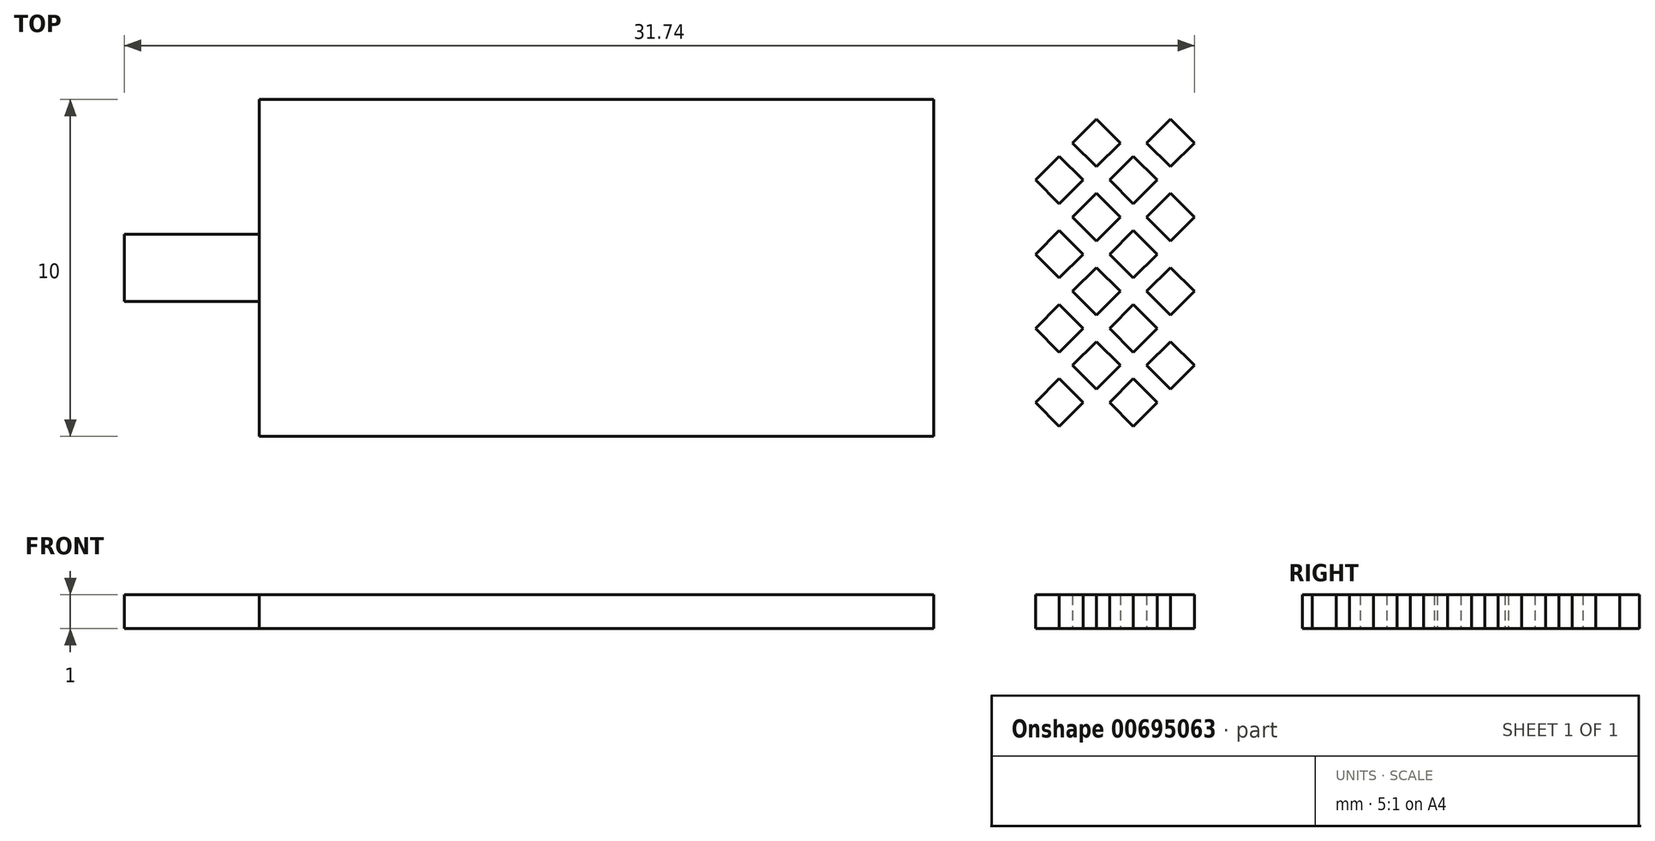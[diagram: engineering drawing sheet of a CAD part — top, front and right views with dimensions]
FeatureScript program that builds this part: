
annotation { "Feature Type Name" : "Feature", "Feature Type Description" : "" }
export const myFeature = defineFeature(function(context is Context, id is Id, definition is map)
    precondition{}
    {
        {
            var Q0;
            Q0=qCreatedBy(makeId("Top.planeOp"),FACE);
            var sketch = newSketch(context, id + "F0", { "sketchPlane" : qUnion([Q0])});
            skLineSegment(sketch, "E0.bottom", {"start": v(0, 0) * mm, "end": v(-20, 0) * mm});
            skLineSegment(sketch, "E0.top", {"start": v(0, 10) * mm, "end": v(-20, 10) * mm});
            skLineSegment(sketch, "E0.left", {"start": v(0, 0) * mm, "end": v(0, 10) * mm});
            skLineSegment(sketch, "E0.right", {"start": v(-20, 0) * mm, "end": v(-20, 10) * mm});
            skSolve(sketch);
        }
        {
            var Q0;
            Q0=qCreatedBy(makeId("Top.planeOp"),FACE);
            var sketch = newSketch(context, id + "F1", { "sketchPlane" : qUnion([Q0])});
            skLineSegment(sketch, "E1.bottom", {"start": v(0, 0) * mm, "end": v(4, 0) * mm});
            skLineSegment(sketch, "E1.top", {"start": v(0, -2) * mm, "end": v(4, -2) * mm});
            skLineSegment(sketch, "E1.left", {"start": v(0, 0) * mm, "end": v(0, -2) * mm});
            skLineSegment(sketch, "E1.right", {"start": v(4, 0) * mm, "end": v(4, -2) * mm});
            skSolve(sketch);
        }
        {
            var Q0;
            Q0=makeQuery(id+"F0.imprint","IMPRINT",FACE,{"disambiguationData":[TD([[makeQuery(id+"F0.imprint","IMPRINT",EDGE,{"derivedFrom":sQuery(id+"F0.wireOp",EDGE,"E0.bottom")}),-1.0]])]});
            extrude(context, id + "F2", {"entities" : qUnion([Q0]), "depth" : 1 * mm, "offsetDistance" : 25 * mm});
        }
        {
            var Q0;
            Q0=makeQuery(id+"F1.imprint","IMPRINT",FACE,{"disambiguationData":[TD([[makeQuery(id+"F1.imprint","IMPRINT",EDGE,{"derivedFrom":sQuery(id+"F1.wireOp",EDGE,"E1.bottom")}),-1.0]])]});
            extrude(context, id + "F3", {"entities" : qUnion([Q0]), "depth" : 1 * mm, "offsetDistance" : 25 * mm});
        }
        {
            var Q0;
            Q0=makeQuery(id+"F3.opExtrude","SWEPT_BODY",BODY,{"disambiguationData":[OSD([sQuery(id+"F1.wireOp",EDGE,"E1.bottom"),sQuery(id+"F1.wireOp",EDGE,"E1.top"),sQuery(id+"F1.wireOp",EDGE,"E1.left"),sQuery(id+"F1.wireOp",EDGE,"E1.right")])]});
            transform(context, id + "F4", {"entities" : qUnion([Q0]), "transformType" : TransformType.TRANSLATION_3D, "dx" : -24 * mm, "dy" : 6 * mm, "dz" : 0 * mm, "makeCopy" : false});
        }
        {
            var Q0;
            Q0=qCreatedBy(makeId("Top.planeOp"),FACE);
            var sketch = newSketch(context, id + "F5", { "sketchPlane" : qUnion([Q0])});
            skLineSegment(sketch, "E2.bottom", {"start": v(3.02, 2) * mm, "end": v(4.02, 2) * mm});
            skLineSegment(sketch, "E2.top", {"start": v(3.02, 1) * mm, "end": v(4.02, 1) * mm});
            skLineSegment(sketch, "E2.left", {"start": v(3.02, 2) * mm, "end": v(3.02, 1) * mm});
            skLineSegment(sketch, "E2.right", {"start": v(4.02, 2) * mm, "end": v(4.02, 1) * mm});
            skSolve(sketch);
        }
        {
            var Q0;
            Q0=makeQuery(id+"F5.imprint","IMPRINT",FACE,{"disambiguationData":[TD([[makeQuery(id+"F5.imprint","IMPRINT",EDGE,{"derivedFrom":sQuery(id+"F5.wireOp",EDGE,"E2.bottom")}),-1.0]])]});
            extrude(context, id + "F6", {"entities" : qUnion([Q0]), "depth" : 1 * mm, "offsetDistance" : 25 * mm});
        }
        {
            var Q0;
            Q0=makeQuery(id+"F6.opExtrude","SWEPT_BODY",BODY,{"disambiguationData":[OSD([sQuery(id+"F5.wireOp",EDGE,"E2.bottom"),sQuery(id+"F5.wireOp",EDGE,"E2.top"),sQuery(id+"F5.wireOp",EDGE,"E2.left"),sQuery(id+"F5.wireOp",EDGE,"E2.right")])]});
            var Q1;
            Q1=makeQuery(id+"F6.opExtrude","SWEPT_EDGE",EDGE,{"disambiguationData":[OSD([sQuery(id+"F5.wireOp",EDGE,"E2.top"),sQuery(id+"F5.wireOp",EDGE,"E2.left")])]});
            transform(context, id + "F7", {"entities" : qUnion([Q0]), "transformType" : TransformType.ROTATION, "transformAxis" : qUnion([Q1]), "angle" : 45 * degree, "makeCopy" : false});
        }
        {
            var Q0;
            Q0=makeQuery(id+"F6.opExtrude","SWEPT_BODY",BODY,{"disambiguationData":[OSD([sQuery(id+"F5.wireOp",EDGE,"E2.bottom"),sQuery(id+"F5.wireOp",EDGE,"E2.top"),sQuery(id+"F5.wireOp",EDGE,"E2.left"),sQuery(id+"F5.wireOp",EDGE,"E2.right")])]});
            transform(context, id + "F8", {"entities" : qUnion([Q0]), "transformType" : TransformType.TRANSLATION_3D, "dx" : 1.1 * mm, "dy" : 1.1 * mm, "dz" : 0 * mm, "makeCopy" : true});
        }
        {
            var Q0;
            Q0=makeQuery(id+"F8.opPattern","COPY",BODY,{"derivedFrom":makeQuery(id+"F6.opExtrude","SWEPT_BODY",BODY,{"disambiguationData":[OSD([sQuery(id+"F5.wireOp",EDGE,"E2.bottom"),sQuery(id+"F5.wireOp",EDGE,"E2.top"),sQuery(id+"F5.wireOp",EDGE,"E2.left"),sQuery(id+"F5.wireOp",EDGE,"E2.right")])]}),"instanceName":"1"});
            transform(context, id + "F9", {"entities" : qUnion([Q0]), "transformType" : TransformType.TRANSLATION_3D, "dx" : -1.1 * mm, "dy" : 1.1 * mm, "dz" : 0 * mm, "makeCopy" : true});
        }
        {
            var Q0;
            Q0=makeQuery(id+"F9.opPattern","COPY",BODY,{"derivedFrom":makeQuery(id+"F8.opPattern","COPY",BODY,{"derivedFrom":makeQuery(id+"F6.opExtrude","SWEPT_BODY",BODY,{"disambiguationData":[OSD([sQuery(id+"F5.wireOp",EDGE,"E2.bottom"),sQuery(id+"F5.wireOp",EDGE,"E2.top"),sQuery(id+"F5.wireOp",EDGE,"E2.left"),sQuery(id+"F5.wireOp",EDGE,"E2.right")])]}),"instanceName":"1"}),"instanceName":"1"});
            var Q1;
            Q1=makeQuery(id+"F8.opPattern","COPY",BODY,{"derivedFrom":makeQuery(id+"F6.opExtrude","SWEPT_BODY",BODY,{"disambiguationData":[OSD([sQuery(id+"F5.wireOp",EDGE,"E2.bottom"),sQuery(id+"F5.wireOp",EDGE,"E2.top"),sQuery(id+"F5.wireOp",EDGE,"E2.left"),sQuery(id+"F5.wireOp",EDGE,"E2.right")])]}),"instanceName":"1"});
            transform(context, id + "F10", {"entities" : qUnion([Q0, Q1]), "transformType" : TransformType.TRANSLATION_3D, "dx" : 0 * mm, "dy" : 2.2 * mm, "dz" : 0 * mm, "makeCopy" : true});
        }
        {
            var Q0;
            Q0=makeQuery(id+"F10.opPattern","COPY",BODY,{"derivedFrom":makeQuery(id+"F9.opPattern","COPY",BODY,{"derivedFrom":makeQuery(id+"F8.opPattern","COPY",BODY,{"derivedFrom":makeQuery(id+"F6.opExtrude","SWEPT_BODY",BODY,{"disambiguationData":[OSD([sQuery(id+"F5.wireOp",EDGE,"E2.bottom"),sQuery(id+"F5.wireOp",EDGE,"E2.top"),sQuery(id+"F5.wireOp",EDGE,"E2.left"),sQuery(id+"F5.wireOp",EDGE,"E2.right")])]}),"instanceName":"1"}),"instanceName":"1"}),"instanceName":"1"});
            var Q1;
            Q1=makeQuery(id+"F10.opPattern","COPY",BODY,{"derivedFrom":makeQuery(id+"F8.opPattern","COPY",BODY,{"derivedFrom":makeQuery(id+"F6.opExtrude","SWEPT_BODY",BODY,{"disambiguationData":[OSD([sQuery(id+"F5.wireOp",EDGE,"E2.bottom"),sQuery(id+"F5.wireOp",EDGE,"E2.top"),sQuery(id+"F5.wireOp",EDGE,"E2.left"),sQuery(id+"F5.wireOp",EDGE,"E2.right")])]}),"instanceName":"1"}),"instanceName":"1"});
            transform(context, id + "F11", {"entities" : qUnion([Q0, Q1]), "transformType" : TransformType.TRANSLATION_3D, "dx" : 0 * mm, "dy" : 2.2 * mm, "dz" : 0 * mm, "makeCopy" : true});
        }
        {
            var Q0;
            Q0=makeQuery(id+"F6.opExtrude","SWEPT_BODY",BODY,{"disambiguationData":[OSD([sQuery(id+"F5.wireOp",EDGE,"E2.bottom"),sQuery(id+"F5.wireOp",EDGE,"E2.top"),sQuery(id+"F5.wireOp",EDGE,"E2.left"),sQuery(id+"F5.wireOp",EDGE,"E2.right")])]});
            transform(context, id + "F12", {"entities" : qUnion([Q0]), "transformType" : TransformType.TRANSLATION_3D, "dx" : 1.1 * mm, "dy" : 7.7 * mm, "dz" : 0 * mm, "makeCopy" : true});
        }
        {
            var Q0;
            Q0=makeQuery(id+"F12.opPattern","COPY",BODY,{"derivedFrom":makeQuery(id+"F6.opExtrude","SWEPT_BODY",BODY,{"disambiguationData":[OSD([sQuery(id+"F5.wireOp",EDGE,"E2.bottom"),sQuery(id+"F5.wireOp",EDGE,"E2.top"),sQuery(id+"F5.wireOp",EDGE,"E2.left"),sQuery(id+"F5.wireOp",EDGE,"E2.right")])]}),"instanceName":"1"});
            var Q1;
            Q1=makeQuery(id+"F11.opPattern","COPY",BODY,{"derivedFrom":makeQuery(id+"F10.opPattern","COPY",BODY,{"derivedFrom":makeQuery(id+"F9.opPattern","COPY",BODY,{"derivedFrom":makeQuery(id+"F8.opPattern","COPY",BODY,{"derivedFrom":makeQuery(id+"F6.opExtrude","SWEPT_BODY",BODY,{"disambiguationData":[OSD([sQuery(id+"F5.wireOp",EDGE,"E2.bottom"),sQuery(id+"F5.wireOp",EDGE,"E2.top"),sQuery(id+"F5.wireOp",EDGE,"E2.left"),sQuery(id+"F5.wireOp",EDGE,"E2.right")])]}),"instanceName":"1"}),"instanceName":"1"}),"instanceName":"1"}),"instanceName":"1"});
            var Q2;
            Q2=makeQuery(id+"F11.opPattern","COPY",BODY,{"derivedFrom":makeQuery(id+"F10.opPattern","COPY",BODY,{"derivedFrom":makeQuery(id+"F8.opPattern","COPY",BODY,{"derivedFrom":makeQuery(id+"F6.opExtrude","SWEPT_BODY",BODY,{"disambiguationData":[OSD([sQuery(id+"F5.wireOp",EDGE,"E2.bottom"),sQuery(id+"F5.wireOp",EDGE,"E2.top"),sQuery(id+"F5.wireOp",EDGE,"E2.left"),sQuery(id+"F5.wireOp",EDGE,"E2.right")])]}),"instanceName":"1"}),"instanceName":"1"}),"instanceName":"1"});
            var Q3;
            Q3=makeQuery(id+"F10.opPattern","COPY",BODY,{"derivedFrom":makeQuery(id+"F9.opPattern","COPY",BODY,{"derivedFrom":makeQuery(id+"F8.opPattern","COPY",BODY,{"derivedFrom":makeQuery(id+"F6.opExtrude","SWEPT_BODY",BODY,{"disambiguationData":[OSD([sQuery(id+"F5.wireOp",EDGE,"E2.bottom"),sQuery(id+"F5.wireOp",EDGE,"E2.top"),sQuery(id+"F5.wireOp",EDGE,"E2.left"),sQuery(id+"F5.wireOp",EDGE,"E2.right")])]}),"instanceName":"1"}),"instanceName":"1"}),"instanceName":"1"});
            var Q4;
            Q4=makeQuery(id+"F10.opPattern","COPY",BODY,{"derivedFrom":makeQuery(id+"F8.opPattern","COPY",BODY,{"derivedFrom":makeQuery(id+"F6.opExtrude","SWEPT_BODY",BODY,{"disambiguationData":[OSD([sQuery(id+"F5.wireOp",EDGE,"E2.bottom"),sQuery(id+"F5.wireOp",EDGE,"E2.top"),sQuery(id+"F5.wireOp",EDGE,"E2.left"),sQuery(id+"F5.wireOp",EDGE,"E2.right")])]}),"instanceName":"1"}),"instanceName":"1"});
            var Q5;
            Q5=makeQuery(id+"F9.opPattern","COPY",BODY,{"derivedFrom":makeQuery(id+"F8.opPattern","COPY",BODY,{"derivedFrom":makeQuery(id+"F6.opExtrude","SWEPT_BODY",BODY,{"disambiguationData":[OSD([sQuery(id+"F5.wireOp",EDGE,"E2.bottom"),sQuery(id+"F5.wireOp",EDGE,"E2.top"),sQuery(id+"F5.wireOp",EDGE,"E2.left"),sQuery(id+"F5.wireOp",EDGE,"E2.right")])]}),"instanceName":"1"}),"instanceName":"1"});
            var Q6;
            Q6=makeQuery(id+"F8.opPattern","COPY",BODY,{"derivedFrom":makeQuery(id+"F6.opExtrude","SWEPT_BODY",BODY,{"disambiguationData":[OSD([sQuery(id+"F5.wireOp",EDGE,"E2.bottom"),sQuery(id+"F5.wireOp",EDGE,"E2.top"),sQuery(id+"F5.wireOp",EDGE,"E2.left"),sQuery(id+"F5.wireOp",EDGE,"E2.right")])]}),"instanceName":"1"});
            var Q7;
            Q7=makeQuery(id+"F6.opExtrude","SWEPT_BODY",BODY,{"disambiguationData":[OSD([sQuery(id+"F5.wireOp",EDGE,"E2.bottom"),sQuery(id+"F5.wireOp",EDGE,"E2.top"),sQuery(id+"F5.wireOp",EDGE,"E2.left"),sQuery(id+"F5.wireOp",EDGE,"E2.right")])]});
            transform(context, id + "F13", {"entities" : qUnion([Q0, Q1, Q2, Q3, Q4, Q5, Q6, Q7]), "transformType" : TransformType.TRANSLATION_3D, "dx" : 2.2 * mm, "dy" : 0 * mm, "dz" : 0 * mm, "makeCopy" : true});
        }
        {
            var Q0;
            Q0=makeQuery(id+"F6.opExtrude","SWEPT_BODY",BODY,{"disambiguationData":[OSD([sQuery(id+"F5.wireOp",EDGE,"E2.bottom"),sQuery(id+"F5.wireOp",EDGE,"E2.top"),sQuery(id+"F5.wireOp",EDGE,"E2.left"),sQuery(id+"F5.wireOp",EDGE,"E2.right")])]});
            var Q1;
            Q1=makeQuery(id+"F8.opPattern","COPY",BODY,{"derivedFrom":makeQuery(id+"F6.opExtrude","SWEPT_BODY",BODY,{"disambiguationData":[OSD([sQuery(id+"F5.wireOp",EDGE,"E2.bottom"),sQuery(id+"F5.wireOp",EDGE,"E2.top"),sQuery(id+"F5.wireOp",EDGE,"E2.left"),sQuery(id+"F5.wireOp",EDGE,"E2.right")])]}),"instanceName":"1"});
            var Q2;
            Q2=makeQuery(id+"F10.opPattern","COPY",BODY,{"derivedFrom":makeQuery(id+"F9.opPattern","COPY",BODY,{"derivedFrom":makeQuery(id+"F8.opPattern","COPY",BODY,{"derivedFrom":makeQuery(id+"F6.opExtrude","SWEPT_BODY",BODY,{"disambiguationData":[OSD([sQuery(id+"F5.wireOp",EDGE,"E2.bottom"),sQuery(id+"F5.wireOp",EDGE,"E2.top"),sQuery(id+"F5.wireOp",EDGE,"E2.left"),sQuery(id+"F5.wireOp",EDGE,"E2.right")])]}),"instanceName":"1"}),"instanceName":"1"}),"instanceName":"1"});
            var Q3;
            Q3=makeQuery(id+"F10.opPattern","COPY",BODY,{"derivedFrom":makeQuery(id+"F8.opPattern","COPY",BODY,{"derivedFrom":makeQuery(id+"F6.opExtrude","SWEPT_BODY",BODY,{"disambiguationData":[OSD([sQuery(id+"F5.wireOp",EDGE,"E2.bottom"),sQuery(id+"F5.wireOp",EDGE,"E2.top"),sQuery(id+"F5.wireOp",EDGE,"E2.left"),sQuery(id+"F5.wireOp",EDGE,"E2.right")])]}),"instanceName":"1"}),"instanceName":"1"});
            var Q4;
            Q4=makeQuery(id+"F9.opPattern","COPY",BODY,{"derivedFrom":makeQuery(id+"F8.opPattern","COPY",BODY,{"derivedFrom":makeQuery(id+"F6.opExtrude","SWEPT_BODY",BODY,{"disambiguationData":[OSD([sQuery(id+"F5.wireOp",EDGE,"E2.bottom"),sQuery(id+"F5.wireOp",EDGE,"E2.top"),sQuery(id+"F5.wireOp",EDGE,"E2.left"),sQuery(id+"F5.wireOp",EDGE,"E2.right")])]}),"instanceName":"1"}),"instanceName":"1"});
            var Q5;
            Q5=makeQuery(id+"F11.opPattern","COPY",BODY,{"derivedFrom":makeQuery(id+"F10.opPattern","COPY",BODY,{"derivedFrom":makeQuery(id+"F8.opPattern","COPY",BODY,{"derivedFrom":makeQuery(id+"F6.opExtrude","SWEPT_BODY",BODY,{"disambiguationData":[OSD([sQuery(id+"F5.wireOp",EDGE,"E2.bottom"),sQuery(id+"F5.wireOp",EDGE,"E2.top"),sQuery(id+"F5.wireOp",EDGE,"E2.left"),sQuery(id+"F5.wireOp",EDGE,"E2.right")])]}),"instanceName":"1"}),"instanceName":"1"}),"instanceName":"1"});
            var Q6;
            Q6=makeQuery(id+"F11.opPattern","COPY",BODY,{"derivedFrom":makeQuery(id+"F10.opPattern","COPY",BODY,{"derivedFrom":makeQuery(id+"F9.opPattern","COPY",BODY,{"derivedFrom":makeQuery(id+"F8.opPattern","COPY",BODY,{"derivedFrom":makeQuery(id+"F6.opExtrude","SWEPT_BODY",BODY,{"disambiguationData":[OSD([sQuery(id+"F5.wireOp",EDGE,"E2.bottom"),sQuery(id+"F5.wireOp",EDGE,"E2.top"),sQuery(id+"F5.wireOp",EDGE,"E2.left"),sQuery(id+"F5.wireOp",EDGE,"E2.right")])]}),"instanceName":"1"}),"instanceName":"1"}),"instanceName":"1"}),"instanceName":"1"});
            var Q7;
            Q7=makeQuery(id+"F12.opPattern","COPY",BODY,{"derivedFrom":makeQuery(id+"F6.opExtrude","SWEPT_BODY",BODY,{"disambiguationData":[OSD([sQuery(id+"F5.wireOp",EDGE,"E2.bottom"),sQuery(id+"F5.wireOp",EDGE,"E2.top"),sQuery(id+"F5.wireOp",EDGE,"E2.left"),sQuery(id+"F5.wireOp",EDGE,"E2.right")])]}),"instanceName":"1"});
            var Q8;
            Q8=makeQuery(id+"F13.opPattern","COPY",BODY,{"derivedFrom":makeQuery(id+"F6.opExtrude","SWEPT_BODY",BODY,{"disambiguationData":[OSD([sQuery(id+"F5.wireOp",EDGE,"E2.bottom"),sQuery(id+"F5.wireOp",EDGE,"E2.top"),sQuery(id+"F5.wireOp",EDGE,"E2.left"),sQuery(id+"F5.wireOp",EDGE,"E2.right")])]}),"instanceName":"1"});
            var Q9;
            Q9=makeQuery(id+"F13.opPattern","COPY",BODY,{"derivedFrom":makeQuery(id+"F8.opPattern","COPY",BODY,{"derivedFrom":makeQuery(id+"F6.opExtrude","SWEPT_BODY",BODY,{"disambiguationData":[OSD([sQuery(id+"F5.wireOp",EDGE,"E2.bottom"),sQuery(id+"F5.wireOp",EDGE,"E2.top"),sQuery(id+"F5.wireOp",EDGE,"E2.left"),sQuery(id+"F5.wireOp",EDGE,"E2.right")])]}),"instanceName":"1"}),"instanceName":"1"});
            var Q10;
            Q10=makeQuery(id+"F13.opPattern","COPY",BODY,{"derivedFrom":makeQuery(id+"F9.opPattern","COPY",BODY,{"derivedFrom":makeQuery(id+"F8.opPattern","COPY",BODY,{"derivedFrom":makeQuery(id+"F6.opExtrude","SWEPT_BODY",BODY,{"disambiguationData":[OSD([sQuery(id+"F5.wireOp",EDGE,"E2.bottom"),sQuery(id+"F5.wireOp",EDGE,"E2.top"),sQuery(id+"F5.wireOp",EDGE,"E2.left"),sQuery(id+"F5.wireOp",EDGE,"E2.right")])]}),"instanceName":"1"}),"instanceName":"1"}),"instanceName":"1"});
            var Q11;
            Q11=makeQuery(id+"F13.opPattern","COPY",BODY,{"derivedFrom":makeQuery(id+"F10.opPattern","COPY",BODY,{"derivedFrom":makeQuery(id+"F8.opPattern","COPY",BODY,{"derivedFrom":makeQuery(id+"F6.opExtrude","SWEPT_BODY",BODY,{"disambiguationData":[OSD([sQuery(id+"F5.wireOp",EDGE,"E2.bottom"),sQuery(id+"F5.wireOp",EDGE,"E2.top"),sQuery(id+"F5.wireOp",EDGE,"E2.left"),sQuery(id+"F5.wireOp",EDGE,"E2.right")])]}),"instanceName":"1"}),"instanceName":"1"}),"instanceName":"1"});
            var Q12;
            Q12=makeQuery(id+"F13.opPattern","COPY",BODY,{"derivedFrom":makeQuery(id+"F10.opPattern","COPY",BODY,{"derivedFrom":makeQuery(id+"F9.opPattern","COPY",BODY,{"derivedFrom":makeQuery(id+"F8.opPattern","COPY",BODY,{"derivedFrom":makeQuery(id+"F6.opExtrude","SWEPT_BODY",BODY,{"disambiguationData":[OSD([sQuery(id+"F5.wireOp",EDGE,"E2.bottom"),sQuery(id+"F5.wireOp",EDGE,"E2.top"),sQuery(id+"F5.wireOp",EDGE,"E2.left"),sQuery(id+"F5.wireOp",EDGE,"E2.right")])]}),"instanceName":"1"}),"instanceName":"1"}),"instanceName":"1"}),"instanceName":"1"});
            var Q13;
            Q13=makeQuery(id+"F13.opPattern","COPY",BODY,{"derivedFrom":makeQuery(id+"F11.opPattern","COPY",BODY,{"derivedFrom":makeQuery(id+"F10.opPattern","COPY",BODY,{"derivedFrom":makeQuery(id+"F8.opPattern","COPY",BODY,{"derivedFrom":makeQuery(id+"F6.opExtrude","SWEPT_BODY",BODY,{"disambiguationData":[OSD([sQuery(id+"F5.wireOp",EDGE,"E2.bottom"),sQuery(id+"F5.wireOp",EDGE,"E2.top"),sQuery(id+"F5.wireOp",EDGE,"E2.left"),sQuery(id+"F5.wireOp",EDGE,"E2.right")])]}),"instanceName":"1"}),"instanceName":"1"}),"instanceName":"1"}),"instanceName":"1"});
            var Q14;
            Q14=makeQuery(id+"F13.opPattern","COPY",BODY,{"derivedFrom":makeQuery(id+"F11.opPattern","COPY",BODY,{"derivedFrom":makeQuery(id+"F10.opPattern","COPY",BODY,{"derivedFrom":makeQuery(id+"F9.opPattern","COPY",BODY,{"derivedFrom":makeQuery(id+"F8.opPattern","COPY",BODY,{"derivedFrom":makeQuery(id+"F6.opExtrude","SWEPT_BODY",BODY,{"disambiguationData":[OSD([sQuery(id+"F5.wireOp",EDGE,"E2.bottom"),sQuery(id+"F5.wireOp",EDGE,"E2.top"),sQuery(id+"F5.wireOp",EDGE,"E2.left"),sQuery(id+"F5.wireOp",EDGE,"E2.right")])]}),"instanceName":"1"}),"instanceName":"1"}),"instanceName":"1"}),"instanceName":"1"}),"instanceName":"1"});
            var Q15;
            Q15=makeQuery(id+"F13.opPattern","COPY",BODY,{"derivedFrom":makeQuery(id+"F12.opPattern","COPY",BODY,{"derivedFrom":makeQuery(id+"F6.opExtrude","SWEPT_BODY",BODY,{"disambiguationData":[OSD([sQuery(id+"F5.wireOp",EDGE,"E2.bottom"),sQuery(id+"F5.wireOp",EDGE,"E2.top"),sQuery(id+"F5.wireOp",EDGE,"E2.left"),sQuery(id+"F5.wireOp",EDGE,"E2.right")])]}),"instanceName":"1"}),"instanceName":"1"});
            transform(context, id + "F14", {"entities" : qUnion([Q0, Q1, Q2, Q3, Q4, Q5, Q6, Q7, Q8, Q9, Q10, Q11, Q12, Q13, Q14, Q15]), "transformType" : TransformType.TRANSLATION_3D, "dx" : -22.5 * mm, "dy" : 0.2 * mm, "dz" : 0 * mm, "makeCopy" : true});
        }
        {
            var Q0;
            Q0=makeQuery(id+"F14.opPattern","COPY",BODY,{"derivedFrom":makeQuery(id+"F13.opPattern","COPY",BODY,{"derivedFrom":makeQuery(id+"F12.opPattern","COPY",BODY,{"derivedFrom":makeQuery(id+"F6.opExtrude","SWEPT_BODY",BODY,{"disambiguationData":[OSD([sQuery(id+"F5.wireOp",EDGE,"E2.bottom"),sQuery(id+"F5.wireOp",EDGE,"E2.top"),sQuery(id+"F5.wireOp",EDGE,"E2.left"),sQuery(id+"F5.wireOp",EDGE,"E2.right")])]}),"instanceName":"1"}),"instanceName":"1"}),"instanceName":"1"});
            var Q1;
            Q1=makeQuery(id+"F14.opPattern","COPY",BODY,{"derivedFrom":makeQuery(id+"F13.opPattern","COPY",BODY,{"derivedFrom":makeQuery(id+"F11.opPattern","COPY",BODY,{"derivedFrom":makeQuery(id+"F10.opPattern","COPY",BODY,{"derivedFrom":makeQuery(id+"F9.opPattern","COPY",BODY,{"derivedFrom":makeQuery(id+"F8.opPattern","COPY",BODY,{"derivedFrom":makeQuery(id+"F6.opExtrude","SWEPT_BODY",BODY,{"disambiguationData":[OSD([sQuery(id+"F5.wireOp",EDGE,"E2.bottom"),sQuery(id+"F5.wireOp",EDGE,"E2.top"),sQuery(id+"F5.wireOp",EDGE,"E2.left"),sQuery(id+"F5.wireOp",EDGE,"E2.right")])]}),"instanceName":"1"}),"instanceName":"1"}),"instanceName":"1"}),"instanceName":"1"}),"instanceName":"1"}),"instanceName":"1"});
            var Q2;
            Q2=makeQuery(id+"F14.opPattern","COPY",BODY,{"derivedFrom":makeQuery(id+"F13.opPattern","COPY",BODY,{"derivedFrom":makeQuery(id+"F11.opPattern","COPY",BODY,{"derivedFrom":makeQuery(id+"F10.opPattern","COPY",BODY,{"derivedFrom":makeQuery(id+"F8.opPattern","COPY",BODY,{"derivedFrom":makeQuery(id+"F6.opExtrude","SWEPT_BODY",BODY,{"disambiguationData":[OSD([sQuery(id+"F5.wireOp",EDGE,"E2.bottom"),sQuery(id+"F5.wireOp",EDGE,"E2.top"),sQuery(id+"F5.wireOp",EDGE,"E2.left"),sQuery(id+"F5.wireOp",EDGE,"E2.right")])]}),"instanceName":"1"}),"instanceName":"1"}),"instanceName":"1"}),"instanceName":"1"}),"instanceName":"1"});
            var Q3;
            Q3=makeQuery(id+"F14.opPattern","COPY",BODY,{"derivedFrom":makeQuery(id+"F13.opPattern","COPY",BODY,{"derivedFrom":makeQuery(id+"F10.opPattern","COPY",BODY,{"derivedFrom":makeQuery(id+"F9.opPattern","COPY",BODY,{"derivedFrom":makeQuery(id+"F8.opPattern","COPY",BODY,{"derivedFrom":makeQuery(id+"F6.opExtrude","SWEPT_BODY",BODY,{"disambiguationData":[OSD([sQuery(id+"F5.wireOp",EDGE,"E2.bottom"),sQuery(id+"F5.wireOp",EDGE,"E2.top"),sQuery(id+"F5.wireOp",EDGE,"E2.left"),sQuery(id+"F5.wireOp",EDGE,"E2.right")])]}),"instanceName":"1"}),"instanceName":"1"}),"instanceName":"1"}),"instanceName":"1"}),"instanceName":"1"});
            var Q4;
            Q4=makeQuery(id+"F14.opPattern","COPY",BODY,{"derivedFrom":makeQuery(id+"F13.opPattern","COPY",BODY,{"derivedFrom":makeQuery(id+"F10.opPattern","COPY",BODY,{"derivedFrom":makeQuery(id+"F8.opPattern","COPY",BODY,{"derivedFrom":makeQuery(id+"F6.opExtrude","SWEPT_BODY",BODY,{"disambiguationData":[OSD([sQuery(id+"F5.wireOp",EDGE,"E2.bottom"),sQuery(id+"F5.wireOp",EDGE,"E2.top"),sQuery(id+"F5.wireOp",EDGE,"E2.left"),sQuery(id+"F5.wireOp",EDGE,"E2.right")])]}),"instanceName":"1"}),"instanceName":"1"}),"instanceName":"1"}),"instanceName":"1"});
            var Q5;
            Q5=makeQuery(id+"F14.opPattern","COPY",BODY,{"derivedFrom":makeQuery(id+"F13.opPattern","COPY",BODY,{"derivedFrom":makeQuery(id+"F9.opPattern","COPY",BODY,{"derivedFrom":makeQuery(id+"F8.opPattern","COPY",BODY,{"derivedFrom":makeQuery(id+"F6.opExtrude","SWEPT_BODY",BODY,{"disambiguationData":[OSD([sQuery(id+"F5.wireOp",EDGE,"E2.bottom"),sQuery(id+"F5.wireOp",EDGE,"E2.top"),sQuery(id+"F5.wireOp",EDGE,"E2.left"),sQuery(id+"F5.wireOp",EDGE,"E2.right")])]}),"instanceName":"1"}),"instanceName":"1"}),"instanceName":"1"}),"instanceName":"1"});
            var Q6;
            Q6=makeQuery(id+"F14.opPattern","COPY",BODY,{"derivedFrom":makeQuery(id+"F10.opPattern","COPY",BODY,{"derivedFrom":makeQuery(id+"F8.opPattern","COPY",BODY,{"derivedFrom":makeQuery(id+"F6.opExtrude","SWEPT_BODY",BODY,{"disambiguationData":[OSD([sQuery(id+"F5.wireOp",EDGE,"E2.bottom"),sQuery(id+"F5.wireOp",EDGE,"E2.top"),sQuery(id+"F5.wireOp",EDGE,"E2.left"),sQuery(id+"F5.wireOp",EDGE,"E2.right")])]}),"instanceName":"1"}),"instanceName":"1"}),"instanceName":"1"});
            var Q7;
            Q7=makeQuery(id+"F14.opPattern","COPY",BODY,{"derivedFrom":makeQuery(id+"F10.opPattern","COPY",BODY,{"derivedFrom":makeQuery(id+"F9.opPattern","COPY",BODY,{"derivedFrom":makeQuery(id+"F8.opPattern","COPY",BODY,{"derivedFrom":makeQuery(id+"F6.opExtrude","SWEPT_BODY",BODY,{"disambiguationData":[OSD([sQuery(id+"F5.wireOp",EDGE,"E2.bottom"),sQuery(id+"F5.wireOp",EDGE,"E2.top"),sQuery(id+"F5.wireOp",EDGE,"E2.left"),sQuery(id+"F5.wireOp",EDGE,"E2.right")])]}),"instanceName":"1"}),"instanceName":"1"}),"instanceName":"1"}),"instanceName":"1"});
            var Q8;
            Q8=makeQuery(id+"F14.opPattern","COPY",BODY,{"derivedFrom":makeQuery(id+"F11.opPattern","COPY",BODY,{"derivedFrom":makeQuery(id+"F10.opPattern","COPY",BODY,{"derivedFrom":makeQuery(id+"F8.opPattern","COPY",BODY,{"derivedFrom":makeQuery(id+"F6.opExtrude","SWEPT_BODY",BODY,{"disambiguationData":[OSD([sQuery(id+"F5.wireOp",EDGE,"E2.bottom"),sQuery(id+"F5.wireOp",EDGE,"E2.top"),sQuery(id+"F5.wireOp",EDGE,"E2.left"),sQuery(id+"F5.wireOp",EDGE,"E2.right")])]}),"instanceName":"1"}),"instanceName":"1"}),"instanceName":"1"}),"instanceName":"1"});
            var Q9;
            Q9=makeQuery(id+"F14.opPattern","COPY",BODY,{"derivedFrom":makeQuery(id+"F11.opPattern","COPY",BODY,{"derivedFrom":makeQuery(id+"F10.opPattern","COPY",BODY,{"derivedFrom":makeQuery(id+"F9.opPattern","COPY",BODY,{"derivedFrom":makeQuery(id+"F8.opPattern","COPY",BODY,{"derivedFrom":makeQuery(id+"F6.opExtrude","SWEPT_BODY",BODY,{"disambiguationData":[OSD([sQuery(id+"F5.wireOp",EDGE,"E2.bottom"),sQuery(id+"F5.wireOp",EDGE,"E2.top"),sQuery(id+"F5.wireOp",EDGE,"E2.left"),sQuery(id+"F5.wireOp",EDGE,"E2.right")])]}),"instanceName":"1"}),"instanceName":"1"}),"instanceName":"1"}),"instanceName":"1"}),"instanceName":"1"});
            var Q10;
            Q10=makeQuery(id+"F14.opPattern","COPY",BODY,{"derivedFrom":makeQuery(id+"F12.opPattern","COPY",BODY,{"derivedFrom":makeQuery(id+"F6.opExtrude","SWEPT_BODY",BODY,{"disambiguationData":[OSD([sQuery(id+"F5.wireOp",EDGE,"E2.bottom"),sQuery(id+"F5.wireOp",EDGE,"E2.top"),sQuery(id+"F5.wireOp",EDGE,"E2.left"),sQuery(id+"F5.wireOp",EDGE,"E2.right")])]}),"instanceName":"1"}),"instanceName":"1"});
            var Q11;
            Q11=makeQuery(id+"F14.opPattern","COPY",BODY,{"derivedFrom":makeQuery(id+"F9.opPattern","COPY",BODY,{"derivedFrom":makeQuery(id+"F8.opPattern","COPY",BODY,{"derivedFrom":makeQuery(id+"F6.opExtrude","SWEPT_BODY",BODY,{"disambiguationData":[OSD([sQuery(id+"F5.wireOp",EDGE,"E2.bottom"),sQuery(id+"F5.wireOp",EDGE,"E2.top"),sQuery(id+"F5.wireOp",EDGE,"E2.left"),sQuery(id+"F5.wireOp",EDGE,"E2.right")])]}),"instanceName":"1"}),"instanceName":"1"}),"instanceName":"1"});
            var Q12;
            Q12=makeQuery(id+"F14.opPattern","COPY",BODY,{"derivedFrom":makeQuery(id+"F8.opPattern","COPY",BODY,{"derivedFrom":makeQuery(id+"F6.opExtrude","SWEPT_BODY",BODY,{"disambiguationData":[OSD([sQuery(id+"F5.wireOp",EDGE,"E2.bottom"),sQuery(id+"F5.wireOp",EDGE,"E2.top"),sQuery(id+"F5.wireOp",EDGE,"E2.left"),sQuery(id+"F5.wireOp",EDGE,"E2.right")])]}),"instanceName":"1"}),"instanceName":"1"});
            var Q13;
            Q13=makeQuery(id+"F14.opPattern","COPY",BODY,{"derivedFrom":makeQuery(id+"F13.opPattern","COPY",BODY,{"derivedFrom":makeQuery(id+"F6.opExtrude","SWEPT_BODY",BODY,{"disambiguationData":[OSD([sQuery(id+"F5.wireOp",EDGE,"E2.bottom"),sQuery(id+"F5.wireOp",EDGE,"E2.top"),sQuery(id+"F5.wireOp",EDGE,"E2.left"),sQuery(id+"F5.wireOp",EDGE,"E2.right")])]}),"instanceName":"1"}),"instanceName":"1"});
            var Q14;
            Q14=makeQuery(id+"F14.opPattern","COPY",BODY,{"derivedFrom":makeQuery(id+"F13.opPattern","COPY",BODY,{"derivedFrom":makeQuery(id+"F8.opPattern","COPY",BODY,{"derivedFrom":makeQuery(id+"F6.opExtrude","SWEPT_BODY",BODY,{"disambiguationData":[OSD([sQuery(id+"F5.wireOp",EDGE,"E2.bottom"),sQuery(id+"F5.wireOp",EDGE,"E2.top"),sQuery(id+"F5.wireOp",EDGE,"E2.left"),sQuery(id+"F5.wireOp",EDGE,"E2.right")])]}),"instanceName":"1"}),"instanceName":"1"}),"instanceName":"1"});
            var Q15;
            Q15=makeQuery(id+"F14.opPattern","COPY",BODY,{"derivedFrom":makeQuery(id+"F6.opExtrude","SWEPT_BODY",BODY,{"disambiguationData":[OSD([sQuery(id+"F5.wireOp",EDGE,"E2.bottom"),sQuery(id+"F5.wireOp",EDGE,"E2.top"),sQuery(id+"F5.wireOp",EDGE,"E2.left"),sQuery(id+"F5.wireOp",EDGE,"E2.right")])]}),"instanceName":"1"});
            var Q16;
            Q16=makeQuery(id+"F3.opExtrude","SWEPT_BODY",BODY,{"disambiguationData":[OSD([sQuery(id+"F1.wireOp",EDGE,"E1.bottom"),sQuery(id+"F1.wireOp",EDGE,"E1.top"),sQuery(id+"F1.wireOp",EDGE,"E1.left"),sQuery(id+"F1.wireOp",EDGE,"E1.right")])]});
            booleanBodies(context, id + "F15", {"operationType" : BooleanOperationType.SUBTRACTION, "tools" : qUnion([Q0, Q1, Q2, Q3, Q4, Q5, Q6, Q7, Q8, Q9, Q10, Q11, Q12, Q13, Q14, Q15]), "targets" : qUnion([Q16])});
        }
    });
